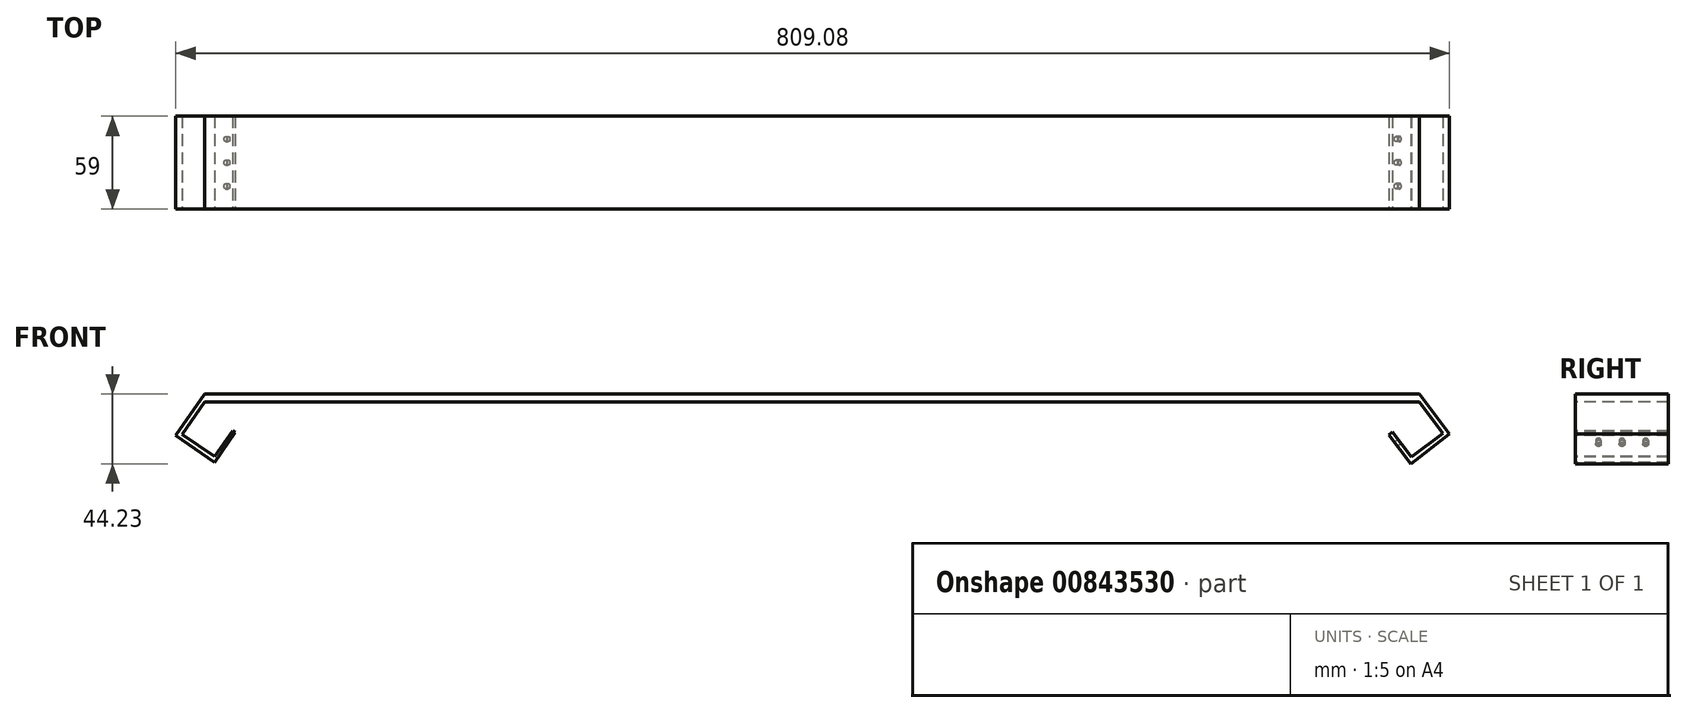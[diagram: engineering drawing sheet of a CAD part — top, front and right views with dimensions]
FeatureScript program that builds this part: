
annotation { "Feature Type Name" : "Feature", "Feature Type Description" : "" }
export const myFeature = defineFeature(function(context is Context, id is Id, definition is map)
    precondition{}
    {
        {
            var Q0;
            Q0=qCreatedBy(makeId("Front.planeOp"),FACE);
            var sketch = newSketch(context, id + "F0", { "sketchPlane" : qUnion([Q0])});
            skLineSegment(sketch, "E0.bottom", {"start": v(385.75, 2.5) * mm, "end": v(-385.75, 2.5) * mm});
            skLineSegment(sketch, "E0.top", {"start": v(385.75, -2.5) * mm, "end": v(-385.75, -2.5) * mm});
            skLineSegment(sketch, "E0.left", {"start": v(385.75, 2.5) * mm, "end": v(385.75, -2.5) * mm});
            skLineSegment(sketch, "E0.right", {"start": v(-385.75, 2.5) * mm, "end": v(-385.75, -2.5) * mm});
            skPoint(sketch, "E0.middle", {"position": v(0, 0) * mm});
            skLineSegment(sketch, "E1", {"start": v(-385.75, 2.5) * mm, "end": v(-402.28, -21.47) * mm});
            skLineSegment(sketch, "E2", {"start": v(-402.28, -21.47) * mm, "end": v(-399.95, -23.08) * mm});
            skLineSegment(sketch, "E3", {"start": v(-399.95, -23.08) * mm, "end": v(-385.75, -2.5) * mm});
            skLineSegment(sketch, "E4", {"start": v(-402.28, -21.47) * mm, "end": v(-403.99, -23.94) * mm});
            skLineSegment(sketch, "E5", {"start": v(-403.99, -23.94) * mm, "end": v(-381.07, -39.74) * mm});
            skLineSegment(sketch, "E6", {"start": v(-381.07, -39.74) * mm, "end": v(-379.37, -37.27) * mm});
            skLineSegment(sketch, "E7", {"start": v(-379.37, -37.27) * mm, "end": v(-402.28, -21.47) * mm});
            skLineSegment(sketch, "E8", {"start": v(385.75, 2.5) * mm, "end": v(403.27, -20.59) * mm});
            skLineSegment(sketch, "E9", {"start": v(403.27, -20.59) * mm, "end": v(400.86, -22.41) * mm});
            skLineSegment(sketch, "E10", {"start": v(400.86, -22.41) * mm, "end": v(385.75, -2.5) * mm});
            skLineSegment(sketch, "E11", {"start": v(403.27, -20.59) * mm, "end": v(405.09, -22.98) * mm});
            skLineSegment(sketch, "E12", {"start": v(405.09, -22.98) * mm, "end": v(382.77, -39.92) * mm});
            skLineSegment(sketch, "E13", {"start": v(382.77, -39.92) * mm, "end": v(380.95, -37.53) * mm});
            skLineSegment(sketch, "E14", {"start": v(380.95, -37.53) * mm, "end": v(400.86, -22.41) * mm});
            skLineSegment(sketch, "E15", {"start": v(-381.07, -39.74) * mm, "end": v(-368.01, -20.81) * mm});
            skLineSegment(sketch, "E16", {"start": v(-368.01, -20.81) * mm, "end": v(-366.3, -21.99) * mm});
            skLineSegment(sketch, "E17", {"start": v(-366.3, -21.99) * mm, "end": v(-379.37, -40.92) * mm});
            skLineSegment(sketch, "E18", {"start": v(-379.37, -40.92) * mm, "end": v(-381.07, -39.74) * mm});
            skLineSegment(sketch, "E19", {"start": v(382.77, -39.92) * mm, "end": v(368.86, -21.6) * mm});
            skLineSegment(sketch, "E20", {"start": v(368.86, -21.6) * mm, "end": v(366.47, -23.41) * mm});
            skLineSegment(sketch, "E21", {"start": v(366.47, -23.41) * mm, "end": v(380.38, -41.73) * mm});
            skLineSegment(sketch, "E22", {"start": v(380.38, -41.73) * mm, "end": v(382.77, -39.92) * mm});
            skSolve(sketch);
        }
        {
            var Q0;
            Q0 = qSketchRegion(id + "F0", true);
            extrude(context, id + "F1", {"entities" : qUnion([Q0]), "oppositeDirection" : true, "depth" : 59 * mm, "offsetDistance" : 25 * mm, "symmetric" : true});
        }
        {
            var Q0;
            Q0=makeQuery(id+"F1.opExtrude","SWEPT_FACE",FACE,{"disambiguationData":[OSD([sQuery(id+"F0.wireOp",EDGE,"E17")])]});
            var sketch = newSketch(context, id + "F2", { "sketchPlane" : qUnion([Q0])});
            skLineSegment(sketch, "E23", {"start": v(-14.75, -233.6) * mm, "end": v(14.75, -233.6) * mm, "construction": true});
            skCircle(sketch, "E24", {"center": v(-15, -233.6) * mm, "radius": 1.65 * mm});
            skCircle(sketch, "E25", {"center": v(0, -233.6) * mm, "radius": 1.65 * mm});
            skCircle(sketch, "E26", {"center": v(15, -233.6) * mm, "radius": 1.65 * mm});
            skSolve(sketch);
        }
        {
            var Q0;
            Q0 = qSketchRegion(id + "F2", true);
            extrude(context, id + "F3", {"entities" : qUnion([Q0]), "operationType" : NewBodyOperationType.REMOVE, "oppositeDirection" : true, "depth" : 3 * mm, "offsetDistance" : 25 * mm});
        }
        {
            var Q0;
            Q0=makeQuery(id+"F1.opExtrude","SWEPT_FACE",FACE,{"disambiguationData":[OSD([sQuery(id+"F0.wireOp",EDGE,"E21")])]});
            var sketch = newSketch(context, id + "F4", { "sketchPlane" : qUnion([Q0])});
            skLineSegment(sketch, "E27", {"start": v(-14.75, -247.72) * mm, "end": v(14.75, -247.72) * mm, "construction": true});
            skCircle(sketch, "E28", {"center": v(0, -247.72) * mm, "radius": 1.65 * mm});
            skCircle(sketch, "E29", {"center": v(-15, -247.72) * mm, "radius": 1.65 * mm});
            skCircle(sketch, "E30", {"center": v(15, -247.72) * mm, "radius": 1.65 * mm});
            skSolve(sketch);
        }
        {
            var Q0;
            Q0 = qSketchRegion(id + "F4", true);
            extrude(context, id + "F5", {"entities" : qUnion([Q0]), "operationType" : NewBodyOperationType.REMOVE, "oppositeDirection" : true, "depth" : 25 * mm, "offsetDistance" : 25 * mm});
        }
    });
